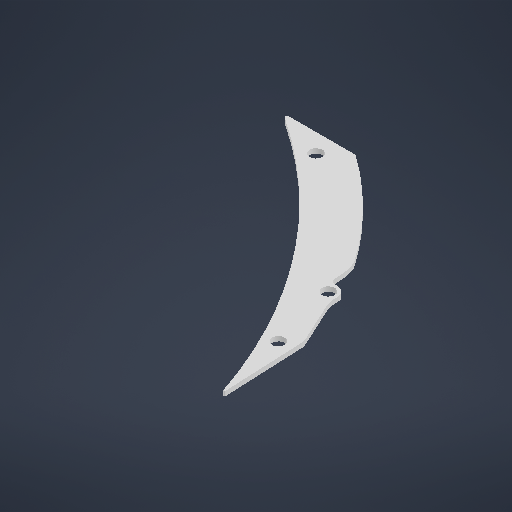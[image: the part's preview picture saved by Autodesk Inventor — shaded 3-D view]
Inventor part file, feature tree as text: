
AUTODESK INVENTOR PART (.ipt)
format: ipt  version: 2025.2 (Build 292293000, 293)  size: 212,992 bytes
history: native  units: in
note: dims shown in document units (in); Inventor stores cm internally (conversion verified against a paired STEP export)
features: extrude x1, sketch x1
ambient origin geometry x8: Origin, YZ Plane, XZ Plane, XY Plane, X Axis, Y Axis, Z Axis, Center Point
bodies: Solid1 (feature_tree)
feature tree (2):
  extrude  "Extrusion1"  Depth=0.0625in
  sketch  "Sketch1"  dims[d5=0.172in d9=0.172in d10=0.172in d12=0.025in d13=0.025in d21=0.0625in d22=0.0in]
